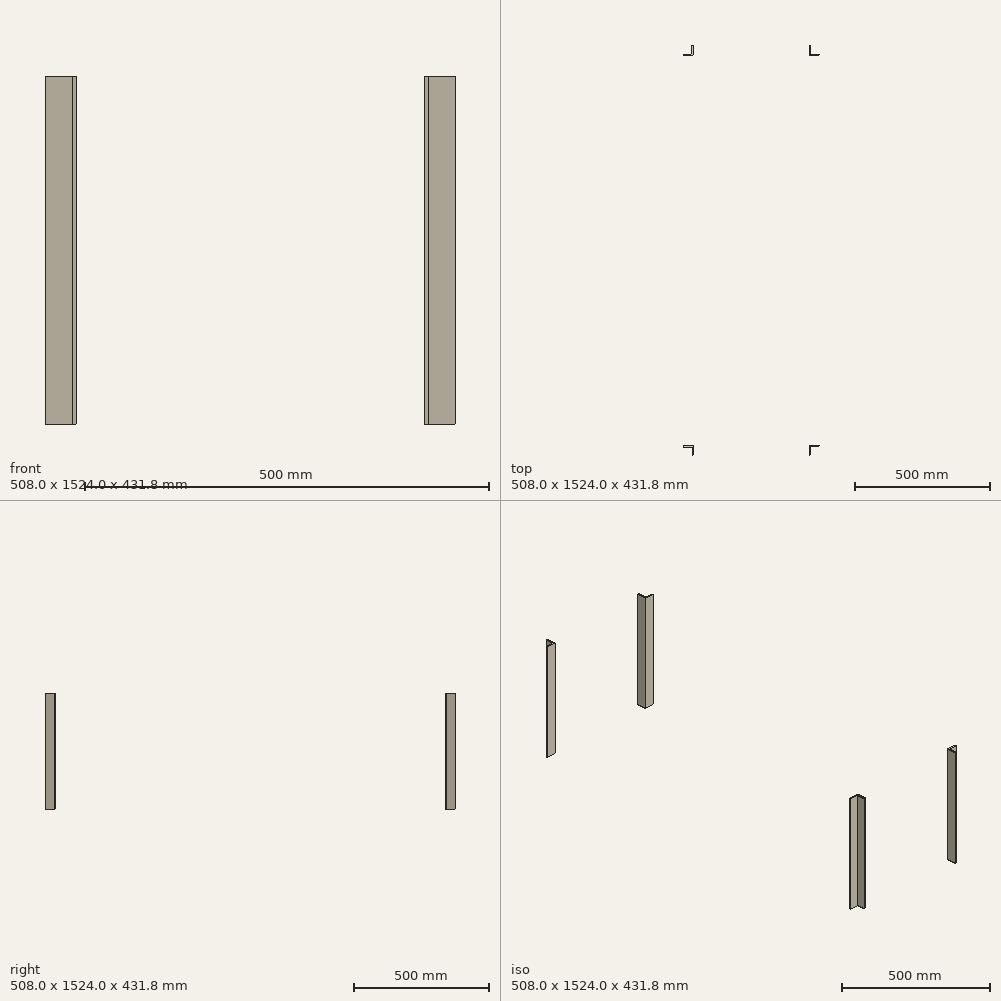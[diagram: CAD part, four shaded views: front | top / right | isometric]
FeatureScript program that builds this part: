
annotation { "Feature Type Name" : "Feature", "Feature Type Description" : "" }
export const myFeature = defineFeature(function(context is Context, id is Id, definition is map)
    precondition{}
    {
        {
            var Q0;
            Q0=qCreatedBy(makeId("Top.planeOp"),FACE);
            var sketch = newSketch(context, id + "F0", { "sketchPlane" : qUnion([Q0])});
            skPoint(sketch, "E0.middle", {"position": v(0, 0) * mm});
            skLineSegment(sketch, "E1.top", {"start": v(-254, 725.05) * mm, "end": v(-216.71, 725.05) * mm});
            skLineSegment(sketch, "E1.right", {"start": v(-216.71, 762) * mm, "end": v(-216.71, 725.05) * mm});
            skLineSegment(sketch, "E2.top", {"start": v(254, 723.82) * mm, "end": v(215.9, 723.82) * mm});
            skLineSegment(sketch, "E2.right", {"start": v(215.9, 762) * mm, "end": v(215.9, 723.82) * mm});
            skLineSegment(sketch, "E3.top", {"start": v(-254, -725.5) * mm, "end": v(-215.87, -725.5) * mm});
            skLineSegment(sketch, "E3.right", {"start": v(-215.87, -762) * mm, "end": v(-215.87, -725.5) * mm});
            skLineSegment(sketch, "E4.top", {"start": v(254, -723.9) * mm, "end": v(215.9, -723.9) * mm});
            skLineSegment(sketch, "E4.right", {"start": v(215.9, -762) * mm, "end": v(215.9, -723.9) * mm});
            skPoint(sketch, "E3.left.start.orphan", {"position": v(-254, -762) * mm});
            skPoint(sketch, "E4.bottom.start.orphan", {"position": v(254, -762) * mm});
            skPoint(sketch, "E5.orphan", {"position": v(-254, 762) * mm});
            skPoint(sketch, "E6.orphan", {"position": v(254, 762) * mm});
            skLineSegment(sketch, "E7.bottom", {"start": v(-216.71, 725.05) * mm, "end": v(-254, 725.05) * mm});
            skLineSegment(sketch, "E7.left", {"start": v(-216.71, 725.05) * mm, "end": v(-216.71, 763.15) * mm});
            skLineSegment(sketch, "E8.bottom", {"start": v(-215.87, -725.5) * mm, "end": v(-254, -725.5) * mm});
            skLineSegment(sketch, "E8.left", {"start": v(-215.87, -725.5) * mm, "end": v(-215.87, -762) * mm});
            skLineSegment(sketch, "E9.bottom", {"start": v(215.9, -723.9) * mm, "end": v(254, -723.9) * mm});
            skLineSegment(sketch, "E9.left", {"start": v(215.9, -723.9) * mm, "end": v(215.9, -762) * mm});
            skLineSegment(sketch, "E10.bottom", {"start": v(220.98, 728.9) * mm, "end": v(254, 728.9) * mm});
            skLineSegment(sketch, "E10.left", {"start": v(220.98, 728.9) * mm, "end": v(220.98, 762) * mm});
            skLineSegment(sketch, "E11.bottom", {"start": v(-221.8, 730.13) * mm, "end": v(-254, 730.13) * mm});
            skLineSegment(sketch, "E11.left", {"start": v(-221.8, 730.13) * mm, "end": v(-221.8, 762) * mm});
            skLineSegment(sketch, "E12.bottom", {"start": v(220.98, -728.98) * mm, "end": v(254, -728.98) * mm});
            skLineSegment(sketch, "E12.left", {"start": v(220.98, -728.98) * mm, "end": v(220.98, -762) * mm});
            skLineSegment(sketch, "E13.bottom", {"start": v(-220.95, -730.59) * mm, "end": v(-254, -730.59) * mm});
            skLineSegment(sketch, "E13.left", {"start": v(-220.95, -730.59) * mm, "end": v(-220.95, -762) * mm});
            skLineSegment(sketch, "E14", {"start": v(-254, -725.5) * mm, "end": v(-254, -730.59) * mm});
            skLineSegment(sketch, "E15", {"start": v(-215.87, -762) * mm, "end": v(-220.95, -762) * mm});
            skLineSegment(sketch, "E16", {"start": v(215.9, -762) * mm, "end": v(220.98, -762) * mm});
            skLineSegment(sketch, "E17", {"start": v(254, -723.9) * mm, "end": v(254, -728.98) * mm});
            skLineSegment(sketch, "E18", {"start": v(215.9, 762) * mm, "end": v(220.98, 762) * mm});
            skLineSegment(sketch, "E19", {"start": v(254, 723.82) * mm, "end": v(254, 728.9) * mm});
            skLineSegment(sketch, "E20", {"start": v(-254, 730.13) * mm, "end": v(-254, 725.05) * mm});
            skLineSegment(sketch, "E21", {"start": v(-216.71, 762) * mm, "end": v(-221.8, 762) * mm});
            skSolve(sketch);
        }
        {
            var Q0;
            Q0=qSketchRegion(id+"F0",true);
            extrude(context, id + "F1", {"entities" : qUnion([Q0]), "depth" : 38.1 * mm, "offsetDistance" : 25.4 * mm});
        }
        {
            var Q0;
            Q0 = qSketchRegion(id + "F0", true);
            extrude(context, id + "F2", {"entities" : qUnion([Q0]), "oppositeDirection" : true, "depth" : 431.8 * mm, "offsetDistance" : 25.4 * mm});
        }
        {
            var Q0;
            Q0=makeQuery(id+"F1.opExtrude","SWEPT_BODY",BODY,{"disambiguationData":[OSD([sQuery(id+"F0.wireOp",EDGE,"E9.bottom"),sQuery(id+"F0.wireOp",EDGE,"E9.left"),sQuery(id+"F0.wireOp",EDGE,"E12.bottom"),sQuery(id+"F0.wireOp",EDGE,"E12.left"),sQuery(id+"F0.wireOp",EDGE,"E16"),sQuery(id+"F0.wireOp",EDGE,"E17")])]});
            deleteBodies(context, id + "F3", {"entities" : qUnion([Q0])});
        }
        {
            var Q0;
            Q0=makeQuery(id+"F1.opExtrude","SWEPT_BODY",BODY,{"disambiguationData":[OSD([sQuery(id+"F0.wireOp",EDGE,"E2.top"),sQuery(id+"F0.wireOp",EDGE,"E2.right"),sQuery(id+"F0.wireOp",EDGE,"E10.bottom"),sQuery(id+"F0.wireOp",EDGE,"E10.left"),sQuery(id+"F0.wireOp",EDGE,"E18"),sQuery(id+"F0.wireOp",EDGE,"E19")])]});
            deleteBodies(context, id + "F4", {"entities" : qUnion([Q0])});
        }
        {
            var Q0;
            Q0=makeQuery(id+"F1.opExtrude","SWEPT_BODY",BODY,{"disambiguationData":[OSD([sQuery(id+"F0.wireOp",EDGE,"E7.bottom"),sQuery(id+"F0.wireOp",EDGE,"E7.left"),sQuery(id+"F0.wireOp",EDGE,"E11.bottom"),sQuery(id+"F0.wireOp",EDGE,"E11.left"),sQuery(id+"F0.wireOp",EDGE,"E20"),sQuery(id+"F0.wireOp",EDGE,"E21")])]});
            deleteBodies(context, id + "F5", {"entities" : qUnion([Q0])});
        }
        {
            var Q0;
            Q0=makeQuery(id+"F1.opExtrude","SWEPT_BODY",BODY,{"disambiguationData":[OSD([sQuery(id+"F0.wireOp",EDGE,"E8.bottom"),sQuery(id+"F0.wireOp",EDGE,"E8.left"),sQuery(id+"F0.wireOp",EDGE,"E13.bottom"),sQuery(id+"F0.wireOp",EDGE,"E13.left"),sQuery(id+"F0.wireOp",EDGE,"E14"),sQuery(id+"F0.wireOp",EDGE,"E15")])]});
            deleteBodies(context, id + "F6", {"entities" : qUnion([Q0])});
        }
    });
